# Revit family: rba-bim-B822
name_source: partatom
category: Specialty Equipment
revit_build: Autodesk Revit 2018 (Build: 20170223_1515(x64)
units: mm (PartAtom-declared; Revit-internal decimal feet)

## family parameters
Cut with Voids When Loaded = No
Host = Face
OmniClass Number = 23.40.20.21.34
OmniClass Title = Soap Holders, Dispensers
Part Type = Normal
Room Calculation Point = No
Round Connector Dimension = Use Diameter
Shared = Yes

## types (4) — shared parameters
ADA Compliant = No
Bottle Material = Plastic Bobrick Soap Dispenser White
Default Elevation = 1.219
Mounting Assembly Material = Plastic Bobrick Soap Dispenser Black
Neck Radius = 0.013
Top Assembly Height = 0.054

## per-type parameters (varying)
| type | Assembly Code | Assembly Depth | Bottle Depth | Bottle Diameter | Bottle Radius | Description | Fixture Material | Manufacturer | Maximum Mounting Depth | Model | Modified Issue | Mounting Depth | Mounting Depth Location | Spout Height | Spout Length | URL |
| B-822 | C1030210 | 0.371 | 0.243 | 0.083 | 0.041 | Basin-Mounted Soap Dispenser | Stainless Steel Bobrick | Bobrick Washroom Equipment, Inc. | 0.102 | B-822 | 20210812.01 | 0.051 | 0.051 | 0.076 | 0.102 | www.rba.com.au |
| B-8221 | C1030210 | 0.21 | 0.156 | 0.083 | 0.041 | Lavatory-Mounted Soap Dispenser | Stainless Steel Bobrick | Bobrick Washroom Equipment, Inc. | 0.025 | B-Series |  | 0.025 | 0.025 | 0.076 | 0.102 | www.bobrick.com |
| B-8226 | C1030210 | 0.371 | 0.243 | 0.083 | 0.041 | Lavatory-Mounted Soap Dispenser | Stainless Steel Bobrick | RBA Group | 0.102 | B-Series |  | 0.051 | 0.051 | 0.098 | 0.152 | www.rba.com.au |
| B-82216 | E1090900 | 0.21 | 0.156 | 0.084 | 0.042 | Bobrick B-82216 Lavatory Mounted Soap Dispenser | Stainless Steel - Bobrick - Black | Bobrick Washroom Equipment, Inc. | 0.102 | B-82216 | 20210812.01 | 0.051 | 0.051 | 0.098 | 0.152 | http://www.bobrick.com |

## geometry (parser evidence)
native form markers: Blend x12, Sweep x4
no freeform markers — native parametric forms only
